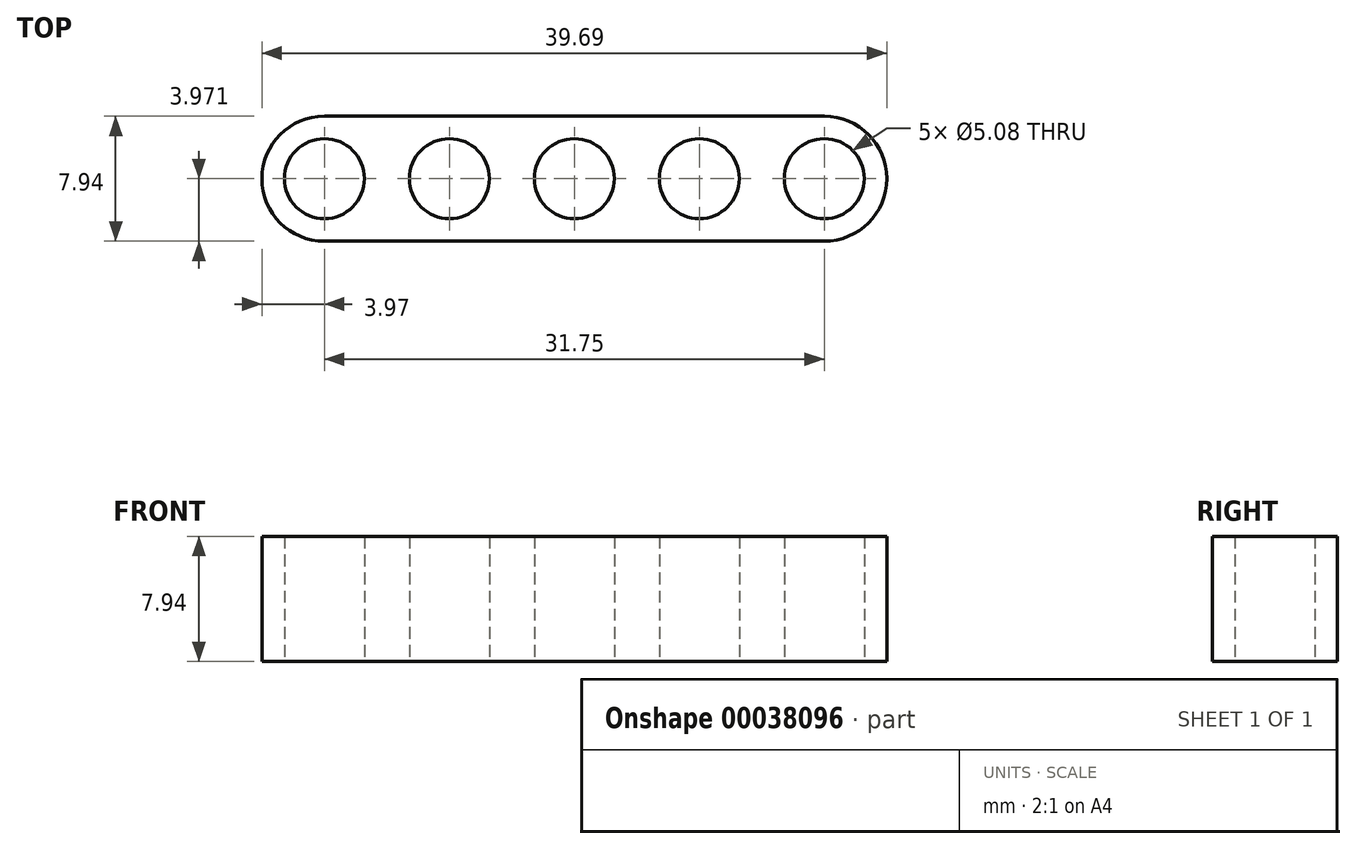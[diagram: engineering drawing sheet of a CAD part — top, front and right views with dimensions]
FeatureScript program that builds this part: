
annotation { "Feature Type Name" : "Feature", "Feature Type Description" : "" }
export const myFeature = defineFeature(function(context is Context, id is Id, definition is map)
    precondition{}
    {
        {
            var Q0;
            Q0=qCreatedBy(makeId("Top.planeOp"),FACE);
            var sketch = newSketch(context, id + "F0", { "sketchPlane" : qUnion([Q0])});
            skLineSegment(sketch, "E0.bottom", {"start": v(0, 0) * mm, "end": v(31.75, 0) * mm});
            skLineSegment(sketch, "E0.top", {"start": v(0, -7.94) * mm, "end": v(31.75, -7.94) * mm});
            skLineSegment(sketch, "E0.left", {"start": v(0, 0) * mm, "end": v(0, -7.94) * mm});
            skLineSegment(sketch, "E0.right", {"start": v(31.75, 0) * mm, "end": v(31.75, -7.94) * mm});
            skLineSegment(sketch, "E1", {"start": v(0, -3.97) * mm, "end": v(7.94, -3.97) * mm, "construction": true});
            skLineSegment(sketch, "E2", {"start": v(7.94, -3.97) * mm, "end": v(15.88, -3.97) * mm, "construction": true});
            skLineSegment(sketch, "E3", {"start": v(15.88, -3.97) * mm, "end": v(23.81, -3.97) * mm, "construction": true});
            skLineSegment(sketch, "E4", {"start": v(23.81, -3.97) * mm, "end": v(31.75, -3.97) * mm, "construction": true});
            skArc(sketch, "E5", {"start": v(0, 0) * mm, "mid": v(-3.97, -3.97) * mm, "end": v(0, -7.94) * mm});
            skArc(sketch, "E6", {"start": v(31.75, -7.94) * mm, "mid": v(35.72, -3.97) * mm, "end": v(31.75, 0) * mm});
            skCircle(sketch, "E7", {"center": v(0, -3.97) * mm, "radius": 2.54 * mm});
            skCircle(sketch, "E8", {"center": v(7.94, -3.97) * mm, "radius": 2.54 * mm});
            skCircle(sketch, "E9", {"center": v(15.88, -3.97) * mm, "radius": 2.54 * mm});
            skCircle(sketch, "E10", {"center": v(23.81, -3.97) * mm, "radius": 2.54 * mm});
            skCircle(sketch, "E11", {"center": v(31.75, -3.97) * mm, "radius": 2.54 * mm});
            skSolve(sketch);
        }
        {
            var Q0;
            Q0 = qSketchRegion(id + "F0", true);
            extrude(context, id + "F1", {"entities" : qUnion([Q0]), "depth" : 7.94 * mm});
        }
    });
